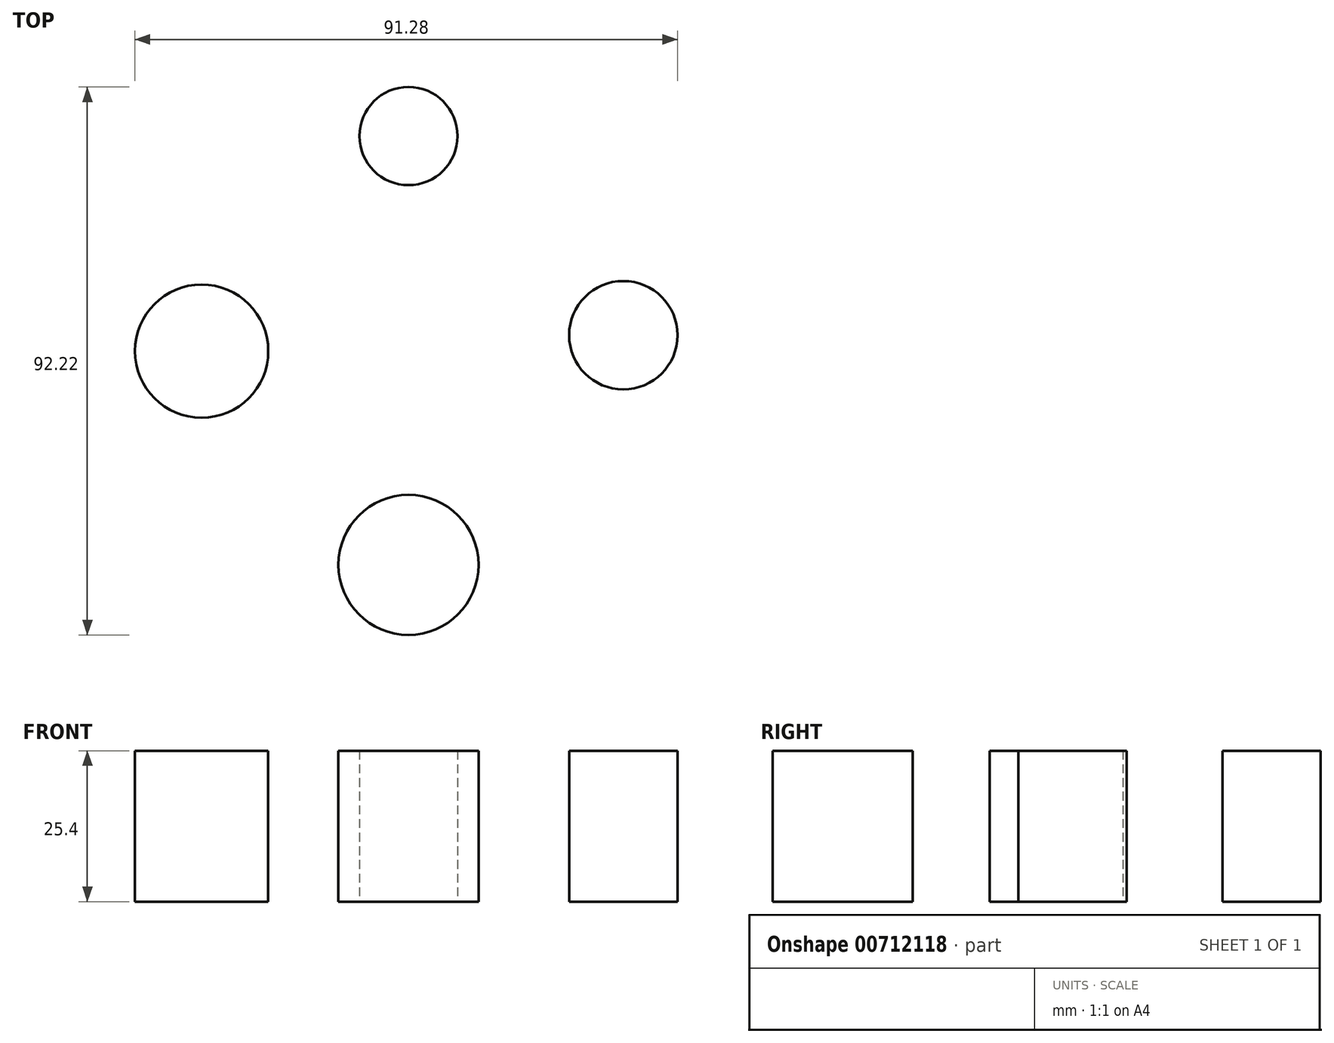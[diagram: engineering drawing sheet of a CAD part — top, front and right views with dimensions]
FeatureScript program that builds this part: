
annotation { "Feature Type Name" : "Feature", "Feature Type Description" : "" }
export const myFeature = defineFeature(function(context is Context, id is Id, definition is map)
    precondition{}
    {
        {
            var Q0;
            Q0=qCreatedBy(makeId("Top.planeOp"),FACE);
            var sketch = newSketch(context, id + "F0", { "sketchPlane" : qUnion([Q0])});
            skCircle(sketch, "E0", {"center": v(0, 0) * mm, "radius": 53.57 * mm});
            skSolve(sketch);
        }
        {
            var Q0;
            Q0=sQuery(id+"F0.wireOp",EDGE,"E0");
            extrude(context, id + "F1", {"bodyType" : ToolBodyType.SURFACE, "surfaceEntities" : qUnion([Q0]), "depth" : 25.4 * mm, "offsetDistance" : 25.4 * mm});
        }
        {
            var Q0;
            Q0=qCreatedBy(makeId("Top.planeOp"),FACE);
            var sketch = newSketch(context, id + "F2", { "sketchPlane" : qUnion([Q0])});
            skCircle(sketch, "E1", {"center": v(36.15, 0) * mm, "radius": 9.12 * mm});
            skSolve(sketch);
        }
        {
            var Q0;
            Q0 = qSketchRegion(id + "F2", true);
            extrude(context, id + "F3", {"entities" : qUnion([Q0]), "depth" : 25.4 * mm, "offsetDistance" : 25.4 * mm});
        }
        {
            var Q0;
            Q0=qCreatedBy(makeId("Top.planeOp"),FACE);
            var sketch = newSketch(context, id + "F4", { "sketchPlane" : qUnion([Q0])});
            skCircle(sketch, "E2", {"center": v(-34.8, -2.68) * mm, "radius": 11.21 * mm});
            skCircle(sketch, "E3", {"center": v(0, -36.48) * mm, "radius": 8.32 * mm});
            skCircle(sketch, "E4", {"center": v(0, 34.9) * mm, "radius": 8.61 * mm});
            skSolve(sketch);
        }
        {
            var Q0;
            Q0=makeQuery(id+"F4.imprint","IMPRINT",FACE,{"disambiguationData":[TD([[makeQuery(id+"F4.imprint","IMPRINT",EDGE,{"derivedFrom":sQuery(id+"F4.wireOp",EDGE,"E2")}),1.0]])]});
            extrude(context, id + "F5", {"entities" : qUnion([Q0]), "depth" : 25.4 * mm, "offsetDistance" : 25.4 * mm});
        }
        {
            var Q0;
            Q0=qCreatedBy(makeId("Top.planeOp"),FACE);
            var sketch = newSketch(context, id + "F6", { "sketchPlane" : qUnion([Q0])});
            skCircle(sketch, "E5", {"center": v(0, -38.66) * mm, "radius": 11.79 * mm});
            skCircle(sketch, "E6", {"center": v(0, 33.52) * mm, "radius": 8.26 * mm});
            skSolve(sketch);
        }
        {
            var Q0;
            Q0 = qSketchRegion(id + "F6", true);
            extrude(context, id + "F7", {"entities" : qUnion([Q0]), "depth" : 25.4 * mm, "offsetDistance" : 25.4 * mm});
        }
    });
